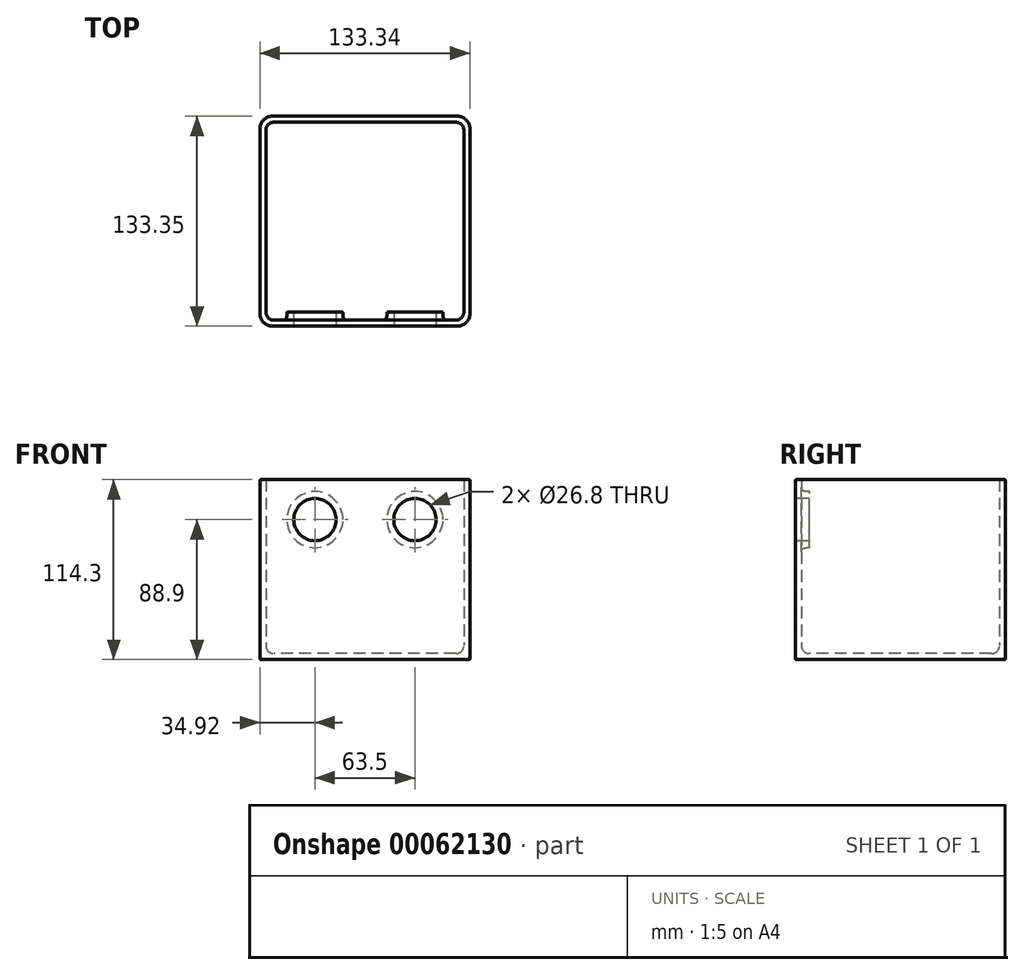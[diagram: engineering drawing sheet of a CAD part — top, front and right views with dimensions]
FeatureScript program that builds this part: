
annotation { "Feature Type Name" : "Feature", "Feature Type Description" : "" }
export const myFeature = defineFeature(function(context is Context, id is Id, definition is map)
    precondition{}
    {
        {
            var Q0;
            Q0=qCreatedBy(makeId("Top.planeOp"),FACE);
            var sketch = newSketch(context, id + "F0", { "sketchPlane" : qUnion([Q0])});
            skLineSegment(sketch, "E0.rect.bottom", {"start": v(66.68, 66.68) * mm, "end": v(-66.68, 66.68) * mm});
            skLineSegment(sketch, "E0.rect.top", {"start": v(66.68, -66.68) * mm, "end": v(-66.68, -66.68) * mm});
            skLineSegment(sketch, "E0.rect.left", {"start": v(66.68, 66.68) * mm, "end": v(66.68, -66.68) * mm});
            skLineSegment(sketch, "E0.rect.right", {"start": v(-66.68, 66.68) * mm, "end": v(-66.68, -66.68) * mm});
            skPoint(sketch, "E0.rect.middle", {"position": v(0, 0) * mm});
            skSolve(sketch);
        }
        {
            var Q0;
            Q0 = qSketchRegion(id + "F0", true);
            extrude(context, id + "F1", {"entities" : qUnion([Q0]), "depth" : 114.3 * mm});
        }
        {
            var Q0;
            Q0=qCreatedBy(makeId("Top.planeOp"),FACE);
            cPlane(context, id + "F2", {"entities" : qUnion([Q0]), "cplaneType" : CPlaneType.OFFSET, "offset" : 3.8 * mm, "width" : 152.4 * mm, "height" : 152.4 * mm});
        }
        {
            var Q0;
            Q0=qCreatedBy(id+"F2.planeOp",FACE);
            var sketch = newSketch(context, id + "F3", { "sketchPlane" : qUnion([Q0])});
            skLineSegment(sketch, "E1.rect.bottom", {"start": v(62.87, 62.87) * mm, "end": v(-62.87, 62.87) * mm});
            skLineSegment(sketch, "E1.rect.top", {"start": v(62.87, -62.87) * mm, "end": v(-62.87, -62.87) * mm});
            skLineSegment(sketch, "E1.rect.left", {"start": v(62.87, 62.87) * mm, "end": v(62.87, -62.87) * mm});
            skLineSegment(sketch, "E1.rect.right", {"start": v(-62.87, 62.87) * mm, "end": v(-62.87, -62.87) * mm});
            skPoint(sketch, "E1.rect.middle", {"position": v(0, 0) * mm});
            skSolve(sketch);
        }
        {
            var Q0;
            Q0 = qSketchRegion(id + "F3", true);
            var Q1;
            Q1=makeQuery(id+"F1.opExtrude","CAP_FACE",FACE,{"disambiguationData":[OSD([sQuery(id+"F0.wireOp",EDGE,"E0.rect.bottom"),sQuery(id+"F0.wireOp",EDGE,"E0.rect.top"),sQuery(id+"F0.wireOp",EDGE,"E0.rect.left"),sQuery(id+"F0.wireOp",EDGE,"E0.rect.right")])],"isStart":false});
            extrude(context, id + "F4", {"entities" : qUnion([Q0]), "operationType" : NewBodyOperationType.REMOVE, "endBound" : BoundingType.UP_TO_SURFACE, "endBoundEntityFace" : qUnion([Q1]), "depth" : 25.4 * mm});
        }
        {
            var Q0;
            Q0=makeQuery(id+"F1.opExtrude","SWEPT_FACE",FACE,{"disambiguationData":[OSD([sQuery(id+"F0.wireOp",EDGE,"E0.rect.top")])]});
            var sketch = newSketch(context, id + "F5", { "sketchPlane" : qUnion([Q0])});
            skCircle(sketch, "E2", {"center": v(-31.75, 88.9) * mm, "radius": 13.4 * mm});
            skCircle(sketch, "E3", {"center": v(31.75, 88.9) * mm, "radius": 13.4 * mm});
            skCircle(sketch, "E4", {"center": v(-31.75, 88.9) * mm, "radius": 17.84 * mm});
            skCircle(sketch, "E5", {"center": v(31.75, 88.9) * mm, "radius": 17.84 * mm});
            skSolve(sketch);
        }
        {
            var Q0;
            Q0=makeQuery(id+"F5.imprint","IMPRINT",FACE,{"disambiguationData":[TD([[makeQuery(id+"F5.imprint","IMPRINT",EDGE,{"derivedFrom":sQuery(id+"F5.wireOp",EDGE,"E2")}),-1.0]])]});
            var Q1;
            Q1=makeQuery(id+"F5.imprint","IMPRINT",FACE,{"disambiguationData":[TD([[makeQuery(id+"F5.imprint","IMPRINT",EDGE,{"derivedFrom":sQuery(id+"F5.wireOp",EDGE,"E3")}),-1.0]])]});
            extrude(context, id + "F6", {"entities" : qUnion([Q0, Q1]), "operationType" : NewBodyOperationType.ADD, "oppositeDirection" : true, "depth" : 8.9 * mm});
        }
        {
            var Q0;
            Q0=makeQuery(id+"F5.imprint","IMPRINT",FACE,{"disambiguationData":[TD([[makeQuery(id+"F5.imprint","IMPRINT",EDGE,{"derivedFrom":sQuery(id+"F5.wireOp",EDGE,"E2")}),1.0]])]});
            var Q1;
            Q1=makeQuery(id+"F5.imprint","IMPRINT",FACE,{"disambiguationData":[TD([[makeQuery(id+"F5.imprint","IMPRINT",EDGE,{"derivedFrom":sQuery(id+"F5.wireOp",EDGE,"E3")}),1.0]])]});
            var Q2;
            {var subQ1=sQuery(id+"F3.wireOp",EDGE,"E1.rect.left");var subQ2=sQuery(id+"F3.wireOp",EDGE,"E1.rect.top");Q2=makeQuery(id+"F6.boolean.opBoolean","SPLIT",FACE,{"disambiguationData":[TD([makeQuery(id+"F4.boolean.opBoolean","COPY",FACE,{"derivedFrom":makeQuery(id+"F4.opExtrude","SWEPT_FACE",FACE,{"disambiguationData":[OSD([subQ1])]})})])],"derivedFrom":makeQuery(id+"F4.boolean.opBoolean","COPY",FACE,{"derivedFrom":makeQuery(id+"F4.opExtrude","SWEPT_FACE",FACE,{"disambiguationData":[OSD([subQ2])]})})});}
            extrude(context, id + "F7", {"entities" : qUnion([Q0, Q1]), "operationType" : NewBodyOperationType.REMOVE, "endBound" : BoundingType.UP_TO_SURFACE, "oppositeDirection" : true, "endBoundEntityFace" : qUnion([Q2]), "depth" : 25.4 * mm});
        }
        {
            var Q0;
            Q0=makeQuery(id+"F4.boolean.opBoolean","COPY",EDGE,{"derivedFrom":makeQuery(id+"F4.opExtrude","CAP_EDGE",EDGE,{"disambiguationData":[OSD([sQuery(id+"F3.wireOp",EDGE,"E1.rect.right")])],"isStart":true})});
            var Q1;
            Q1=makeQuery(id+"F4.boolean.opBoolean","COPY",EDGE,{"derivedFrom":makeQuery(id+"F4.opExtrude","CAP_EDGE",EDGE,{"disambiguationData":[OSD([sQuery(id+"F3.wireOp",EDGE,"E1.rect.bottom")])],"isStart":true})});
            var Q2;
            Q2=makeQuery(id+"F4.boolean.opBoolean","COPY",EDGE,{"derivedFrom":makeQuery(id+"F4.opExtrude","CAP_EDGE",EDGE,{"disambiguationData":[OSD([sQuery(id+"F3.wireOp",EDGE,"E1.rect.left")])],"isStart":true})});
            var Q3;
            Q3=makeQuery(id+"F4.boolean.opBoolean","COPY",EDGE,{"derivedFrom":makeQuery(id+"F4.opExtrude","CAP_EDGE",EDGE,{"disambiguationData":[OSD([sQuery(id+"F3.wireOp",EDGE,"E1.rect.top")])],"isStart":true})});
            var Q4;
            Q4=makeQuery(id+"F4.boolean.opBoolean","COPY",EDGE,{"derivedFrom":makeQuery(id+"F4.opExtrude","SWEPT_EDGE",EDGE,{"disambiguationData":[OSD([sQuery(id+"F3.wireOp",EDGE,"E1.rect.top"),sQuery(id+"F3.wireOp",EDGE,"E1.rect.left")])]})});
            var Q5;
            Q5=makeQuery(id+"F4.boolean.opBoolean","COPY",EDGE,{"derivedFrom":makeQuery(id+"F4.opExtrude","SWEPT_EDGE",EDGE,{"disambiguationData":[OSD([sQuery(id+"F3.wireOp",EDGE,"E1.rect.top"),sQuery(id+"F3.wireOp",EDGE,"E1.rect.right")])]})});
            var Q6;
            Q6=makeQuery(id+"F4.boolean.opBoolean","COPY",EDGE,{"derivedFrom":makeQuery(id+"F4.opExtrude","SWEPT_EDGE",EDGE,{"disambiguationData":[OSD([sQuery(id+"F3.wireOp",EDGE,"E1.rect.bottom"),sQuery(id+"F3.wireOp",EDGE,"E1.rect.right")])]})});
            var Q7;
            Q7=makeQuery(id+"F4.boolean.opBoolean","COPY",EDGE,{"derivedFrom":makeQuery(id+"F4.opExtrude","SWEPT_EDGE",EDGE,{"disambiguationData":[OSD([sQuery(id+"F3.wireOp",EDGE,"E1.rect.bottom"),sQuery(id+"F3.wireOp",EDGE,"E1.rect.left")])]})});
            fillet(context, id + "F8", {"entities" : qUnion([Q0, Q1, Q2, Q3, Q4, Q5, Q6, Q7]), "radius" : 5.08 * mm, "tangentPropagation" : true, "allowEdgeOverflow" : false});
        }
        {
            var Q0;
            Q0=makeQuery(id+"F1.opExtrude","SWEPT_EDGE",EDGE,{"disambiguationData":[OSD([sQuery(id+"F0.wireOp",EDGE,"E0.rect.bottom"),sQuery(id+"F0.wireOp",EDGE,"E0.rect.right")])]});
            var Q1;
            Q1=makeQuery(id+"F1.opExtrude","SWEPT_EDGE",EDGE,{"disambiguationData":[OSD([sQuery(id+"F0.wireOp",EDGE,"E0.rect.bottom"),sQuery(id+"F0.wireOp",EDGE,"E0.rect.left")])]});
            var Q2;
            Q2=makeQuery(id+"F1.opExtrude","SWEPT_EDGE",EDGE,{"disambiguationData":[OSD([sQuery(id+"F0.wireOp",EDGE,"E0.rect.top"),sQuery(id+"F0.wireOp",EDGE,"E0.rect.right")])]});
            var Q3;
            Q3=makeQuery(id+"F1.opExtrude","SWEPT_EDGE",EDGE,{"disambiguationData":[OSD([sQuery(id+"F0.wireOp",EDGE,"E0.rect.top"),sQuery(id+"F0.wireOp",EDGE,"E0.rect.left")])]});
            fillet(context, id + "F9", {"entities" : qUnion([Q0, Q1, Q2, Q3]), "radius" : 8 * mm, "tangentPropagation" : true, "allowEdgeOverflow" : false});
        }
        {
            var Q0;
            Q0=makeQuery(id+"F7.boolean.opBoolean","COPY",EDGE,{"derivedFrom":makeQuery(id+"F7.opExtrude","CAP_EDGE",EDGE,{"disambiguationData":[OSD([sQuery(id+"F5.wireOp",EDGE,"E2")])],"isStart":true})});
            var Q1;
            Q1=makeQuery(id+"F7.boolean.opBoolean","COPY",EDGE,{"derivedFrom":makeQuery(id+"F7.opExtrude","CAP_EDGE",EDGE,{"disambiguationData":[OSD([sQuery(id+"F5.wireOp",EDGE,"E3")])],"isStart":true})});
            var Q2;
            Q2=makeQuery(id+"F6.opExtrude","CAP_EDGE",EDGE,{"disambiguationData":[OSD([sQuery(id+"F5.wireOp",EDGE,"E2")])],"isStart":false});
            var Q3;
            Q3=makeQuery(id+"F6.opExtrude","CAP_EDGE",EDGE,{"disambiguationData":[OSD([sQuery(id+"F5.wireOp",EDGE,"E3")])],"isStart":false});
            var Q4;
            {var subQ0=sQuery(id+"F5.wireOp",EDGE,"E5");Q4=makeQuery(id+"F8.opFillet","BLEND_EDGE",EDGE,{"blendedFrom":[makeQuery(id+"F6.boolean.opBoolean","INTERSECT",EDGE,{"derivedFrom":[makeQuery(id+"F4.boolean.opBoolean","COPY",FACE,{"derivedFrom":makeQuery(id+"F4.opExtrude","SWEPT_FACE",FACE,{"disambiguationData":[OSD([sQuery(id+"F3.wireOp",EDGE,"E1.rect.top")])]})}),makeQuery(id+"F6.opExtrude","SWEPT_FACE",FACE,{"disambiguationData":[OSD([subQ0])]})]}),makeQuery(id+"F6.opExtrude","CAP_FACE",FACE,{"disambiguationData":[OSD([sQuery(id+"F5.wireOp",EDGE,"E3"),subQ0])],"isStart":false})],"blendedInto":[makeQuery(id+"F6.opExtrude","CAP_FACE",FACE,{"disambiguationData":[OSD([sQuery(id+"F5.wireOp",EDGE,"E3"),subQ0])],"isStart":false})]});}
            var Q5;
            {var subQ0=sQuery(id+"F5.wireOp",EDGE,"E4");Q5=makeQuery(id+"F8.opFillet","BLEND_EDGE",EDGE,{"blendedFrom":[makeQuery(id+"F6.boolean.opBoolean","INTERSECT",EDGE,{"derivedFrom":[makeQuery(id+"F4.boolean.opBoolean","COPY",FACE,{"derivedFrom":makeQuery(id+"F4.opExtrude","SWEPT_FACE",FACE,{"disambiguationData":[OSD([sQuery(id+"F3.wireOp",EDGE,"E1.rect.top")])]})}),makeQuery(id+"F6.opExtrude","SWEPT_FACE",FACE,{"disambiguationData":[OSD([subQ0])]})]}),makeQuery(id+"F6.opExtrude","CAP_FACE",FACE,{"disambiguationData":[OSD([sQuery(id+"F5.wireOp",EDGE,"E2"),subQ0])],"isStart":false})],"blendedInto":[makeQuery(id+"F6.opExtrude","CAP_FACE",FACE,{"disambiguationData":[OSD([sQuery(id+"F5.wireOp",EDGE,"E2"),subQ0])],"isStart":false})]});}
            fillet(context, id + "F10", {"entities" : qUnion([Q0, Q1, Q2, Q3, Q4, Q5]), "radius" : 0.5 * mm, "tangentPropagation" : true, "allowEdgeOverflow" : false});
        }
        {
            var Q0;
            Q0=makeQuery(id+"F6.boolean.opBoolean","INTERSECT",EDGE,{"derivedFrom":[makeQuery(id+"F4.boolean.opBoolean","COPY",FACE,{"derivedFrom":makeQuery(id+"F4.opExtrude","SWEPT_FACE",FACE,{"disambiguationData":[OSD([sQuery(id+"F3.wireOp",EDGE,"E1.rect.top")])]})}),makeQuery(id+"F6.opExtrude","SWEPT_FACE",FACE,{"disambiguationData":[OSD([sQuery(id+"F5.wireOp",EDGE,"E4")])]})]});
            var Q1;
            Q1=makeQuery(id+"F6.boolean.opBoolean","INTERSECT",EDGE,{"derivedFrom":[makeQuery(id+"F4.boolean.opBoolean","COPY",FACE,{"derivedFrom":makeQuery(id+"F4.opExtrude","SWEPT_FACE",FACE,{"disambiguationData":[OSD([sQuery(id+"F3.wireOp",EDGE,"E1.rect.top")])]})}),makeQuery(id+"F6.opExtrude","SWEPT_FACE",FACE,{"disambiguationData":[OSD([sQuery(id+"F5.wireOp",EDGE,"E5")])]})]});
            fillet(context, id + "F11", {"entities" : qUnion([Q0, Q1]), "radius" : 2.54 * mm, "tangentPropagation" : true, "allowEdgeOverflow" : false});
        }
        {
            var Q0;
            Q0=makeQuery(id+"F1.opExtrude","CAP_EDGE",EDGE,{"disambiguationData":[OSD([sQuery(id+"F0.wireOp",EDGE,"E0.rect.right")])],"isStart":false});
            var Q1;
            Q1=makeQuery(id+"F1.opExtrude","CAP_EDGE",EDGE,{"disambiguationData":[OSD([sQuery(id+"F0.wireOp",EDGE,"E0.rect.right")])],"isStart":true});
            var Q2;
            Q2=makeQuery(id+"F4.boolean.opBoolean","COPY",EDGE,{"derivedFrom":makeQuery(id+"F4.opExtrude","CAP_EDGE",EDGE,{"disambiguationData":[OSD([sQuery(id+"F3.wireOp",EDGE,"E1.rect.right")])],"isStart":false})});
            var Q3;
            Q3=makeQuery(id+"F6.opExtrude","CAP_EDGE",EDGE,{"disambiguationData":[OSD([sQuery(id+"F5.wireOp",EDGE,"E4")])],"isStart":false});
            fillet(context, id + "F12", {"entities" : qUnion([Q0, Q1, Q2, Q3]), "radius" : 0.5 * mm, "tangentPropagation" : true, "allowEdgeOverflow" : false});
        }
    });
